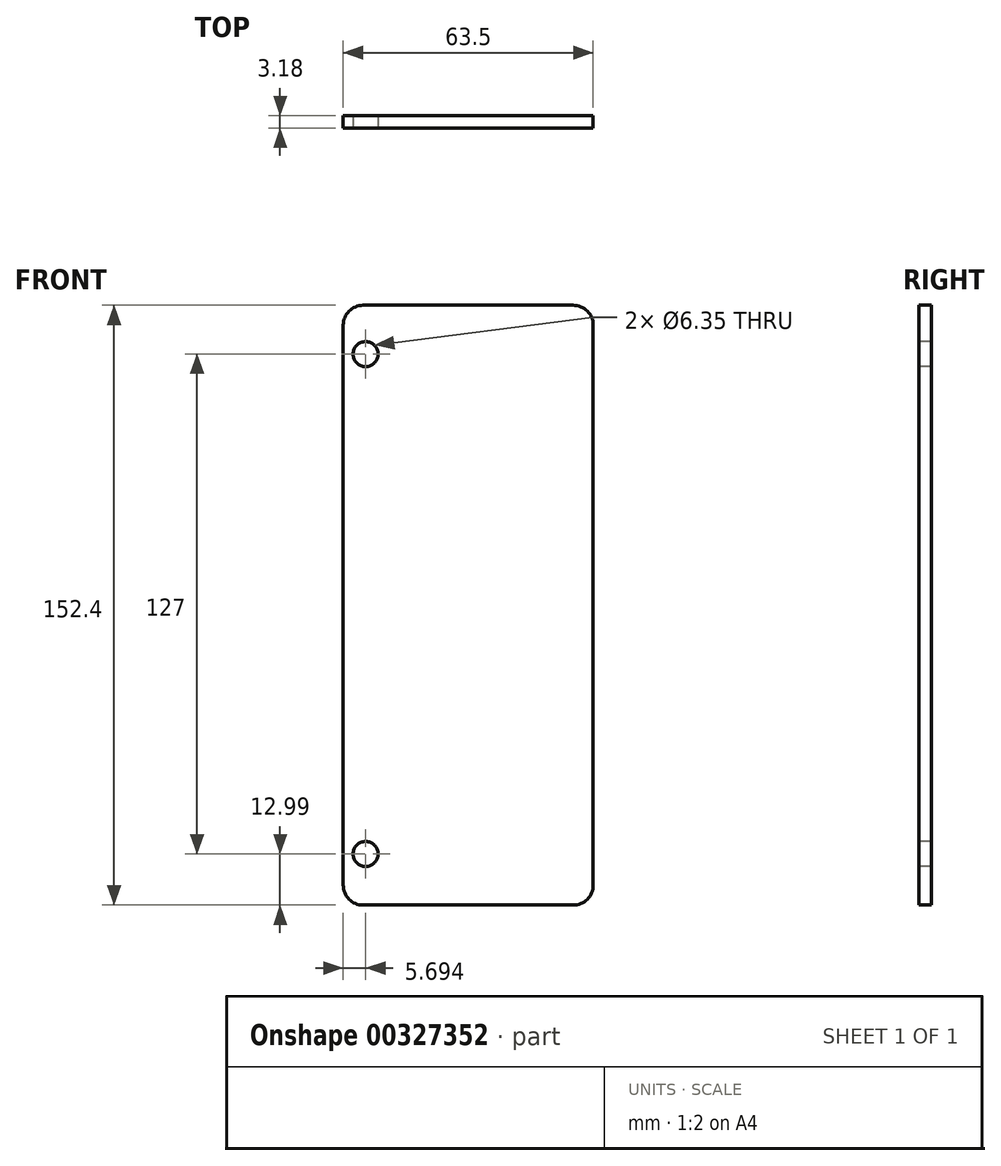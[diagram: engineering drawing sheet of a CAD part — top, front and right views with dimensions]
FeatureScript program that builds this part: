
annotation { "Feature Type Name" : "Feature", "Feature Type Description" : "" }
export const myFeature = defineFeature(function(context is Context, id is Id, definition is map)
    precondition{}
    {
        {
            var Q0;
            Q0=qCreatedBy(makeId("Front.planeOp"),FACE);
            var sketch = newSketch(context, id + "F0", { "sketchPlane" : qUnion([Q0])});
            skLineSegment(sketch, "E0.bottom", {"start": v(-19.73, 108.39) * mm, "end": v(43.77, 108.39) * mm});
            skLineSegment(sketch, "E0.top", {"start": v(-19.73, -44.01) * mm, "end": v(43.77, -44.01) * mm});
            skLineSegment(sketch, "E0.left", {"start": v(-19.73, 108.39) * mm, "end": v(-19.73, -44.01) * mm});
            skLineSegment(sketch, "E0.right", {"start": v(43.77, 108.39) * mm, "end": v(43.77, -44.01) * mm});
            skSolve(sketch);
        }
        {
            var Q0;
            Q0 = qSketchRegion(id + "F0", true);
            var Q1;
            Q1=makeQuery(id+"F0.imprint","IMPRINT",FACE,{"disambiguationData":[TD([[makeQuery(id+"F0.imprint","IMPRINT",EDGE,{"derivedFrom":sQuery(id+"F0.wireOp",EDGE,"E0.bottom")}),-1.0]])]});
            extrude(context, id + "F1", {"entities" : qUnion([Q0, Q1]), "depth" : 3.17 * mm});
        }
        {
            var Q0;
            Q0=makeQuery(id+"F1.opExtrude","SWEPT_EDGE",EDGE,{"disambiguationData":[OSD([sQuery(id+"F0.wireOp",EDGE,"E0.bottom"),sQuery(id+"F0.wireOp",EDGE,"E0.left")])]});
            var Q1;
            Q1=makeQuery(id+"F1.opExtrude","SWEPT_EDGE",EDGE,{"disambiguationData":[OSD([sQuery(id+"F0.wireOp",EDGE,"E0.bottom"),sQuery(id+"F0.wireOp",EDGE,"E0.right")])]});
            var Q2;
            Q2=makeQuery(id+"F1.opExtrude","SWEPT_EDGE",EDGE,{"disambiguationData":[OSD([sQuery(id+"F0.wireOp",EDGE,"E0.top"),sQuery(id+"F0.wireOp",EDGE,"E0.right")])]});
            var Q3;
            Q3=makeQuery(id+"F1.opExtrude","SWEPT_EDGE",EDGE,{"disambiguationData":[OSD([sQuery(id+"F0.wireOp",EDGE,"E0.top"),sQuery(id+"F0.wireOp",EDGE,"E0.left")])]});
            fillet(context, id + "F2", {"entities" : qUnion([Q0, Q1, Q2, Q3]), "radius" : 5.08 * mm, "tangentPropagation" : true, "allowEdgeOverflow" : false});
        }
        {
            var Q0;
            Q0=makeQuery(id+"F1.opExtrude","CAP_FACE",FACE,{"disambiguationData":[OSD([sQuery(id+"F0.wireOp",EDGE,"E0.bottom"),sQuery(id+"F0.wireOp",EDGE,"E0.top"),sQuery(id+"F0.wireOp",EDGE,"E0.left"),sQuery(id+"F0.wireOp",EDGE,"E0.right")])],"isStart":false});
            var sketch = newSketch(context, id + "F3", { "sketchPlane" : qUnion([Q0])});
            skLineSegment(sketch, "E1.bottom", {"start": v(-14.04, 95.98) * mm, "end": v(36.76, 95.98) * mm});
            skLineSegment(sketch, "E1.top", {"start": v(-14.04, -31.02) * mm, "end": v(36.76, -31.02) * mm});
            skLineSegment(sketch, "E1.left", {"start": v(-14.04, 95.98) * mm, "end": v(-14.04, -31.02) * mm});
            skLineSegment(sketch, "E1.right", {"start": v(36.76, 95.98) * mm, "end": v(36.76, -31.02) * mm});
            skSolve(sketch);
        }
        {
            var Q0;
            Q0=sQuery(id+"F3.wireOp",VERTEX,"E1.bottom.start");
            var Q1;
            Q1=makeQuery(id+"F1.opExtrude","SWEPT_BODY",BODY,{"disambiguationData":[OSD([sQuery(id+"F0.wireOp",EDGE,"E0.bottom"),sQuery(id+"F0.wireOp",EDGE,"E0.top"),sQuery(id+"F0.wireOp",EDGE,"E0.left"),sQuery(id+"F0.wireOp",EDGE,"E0.right")])]});
            hole(context, id + "F4", {"style" : HoleStyle.SIMPLE, "endStyle" : HoleEndStyle.THROUGH, "holeDiameter" : 6.35 * mm, "tappedDepth" : 12.7 * mm, "tapClearance" : 3, "locations" : qUnion([Q0]), "scope" : qUnion([Q1])});
        }
        {
            var Q0;
            Q0=sQuery(id+"F3.wireOp",VERTEX,"E1.left.end");
            var Q1;
            Q1=makeQuery(id+"F1.opExtrude","SWEPT_BODY",BODY,{"disambiguationData":[OSD([sQuery(id+"F0.wireOp",EDGE,"E0.bottom"),sQuery(id+"F0.wireOp",EDGE,"E0.top"),sQuery(id+"F0.wireOp",EDGE,"E0.left"),sQuery(id+"F0.wireOp",EDGE,"E0.right")])]});
            hole(context, id + "F5", {"style" : HoleStyle.SIMPLE, "endStyle" : HoleEndStyle.THROUGH, "holeDiameter" : 6.35 * mm, "tappedDepth" : 12.7 * mm, "tapClearance" : 3, "locations" : qUnion([Q0]), "scope" : qUnion([Q1])});
        }
    });
